# Revit family: Gewindeplatte 40x22
name_source: partatom
category: HLS-Bauteile
revit_build: Autodesk Revit 2017 (Build: 20190507_1515(x64)
units: mm (PartAtom-declared; Revit-internal decimal feet)

## family parameters
Arbeitsebenenbasiert = Ja
Beim Laden mit Abzugskörper schneiden = Nein
Bemaßung runder Anschluss = Durchmesser verwenden
Gemeinsam genutzt = Ja
Immer vertikal = Nein
Raumberechnungspunkt = Nein
Teiletyp = Normal

## types (1)
- Gewindeplatte 40x22 M12
    Abmessung = 40x22 mm
    Anzugsmoment = 0
    Anzugsmoment XL100 = 0.00 kN-m
    Anzugsmoment XL80 = 0.00 kN-m
    Artikelnummer = 0750123
    Breite = 0 mm  [stored 0 ft]
    EAN = 4250928417183
    Fabrikat = MEFA
    Firma = MEFA Befestigungs- und Montagesysteme GmbH
    Gewicht = 0.0391
    Gewinde = M12
    Kurztext1 = Gewindeplatte
    Kurztext2 = M12 40x22 gvz
    Länge = 0 mm  [stored 0 ft]
    Länge Gewinde = 0 mm  [stored 0 ft]
    Material = Stahl
    Materialname = S235
    Mengeneinheit = St
    Oberflaeche = galvanisch verzinkt
    Preiseinheit = 0
    Profil = C-Profil
    Profiltyp = 45
    Stärke Material = 0 mm  [stored 0 ft]
    Vorgabe-Ansicht = 1219 mm
    d2 = 6 mm  [stored 0.019685 ft]
    max. zul. Last = 0
    vpe = 100 St

note: [stored X ft] marks values corroborated as IEEE doubles in the binary element streams (Revit-internal decimal feet)
